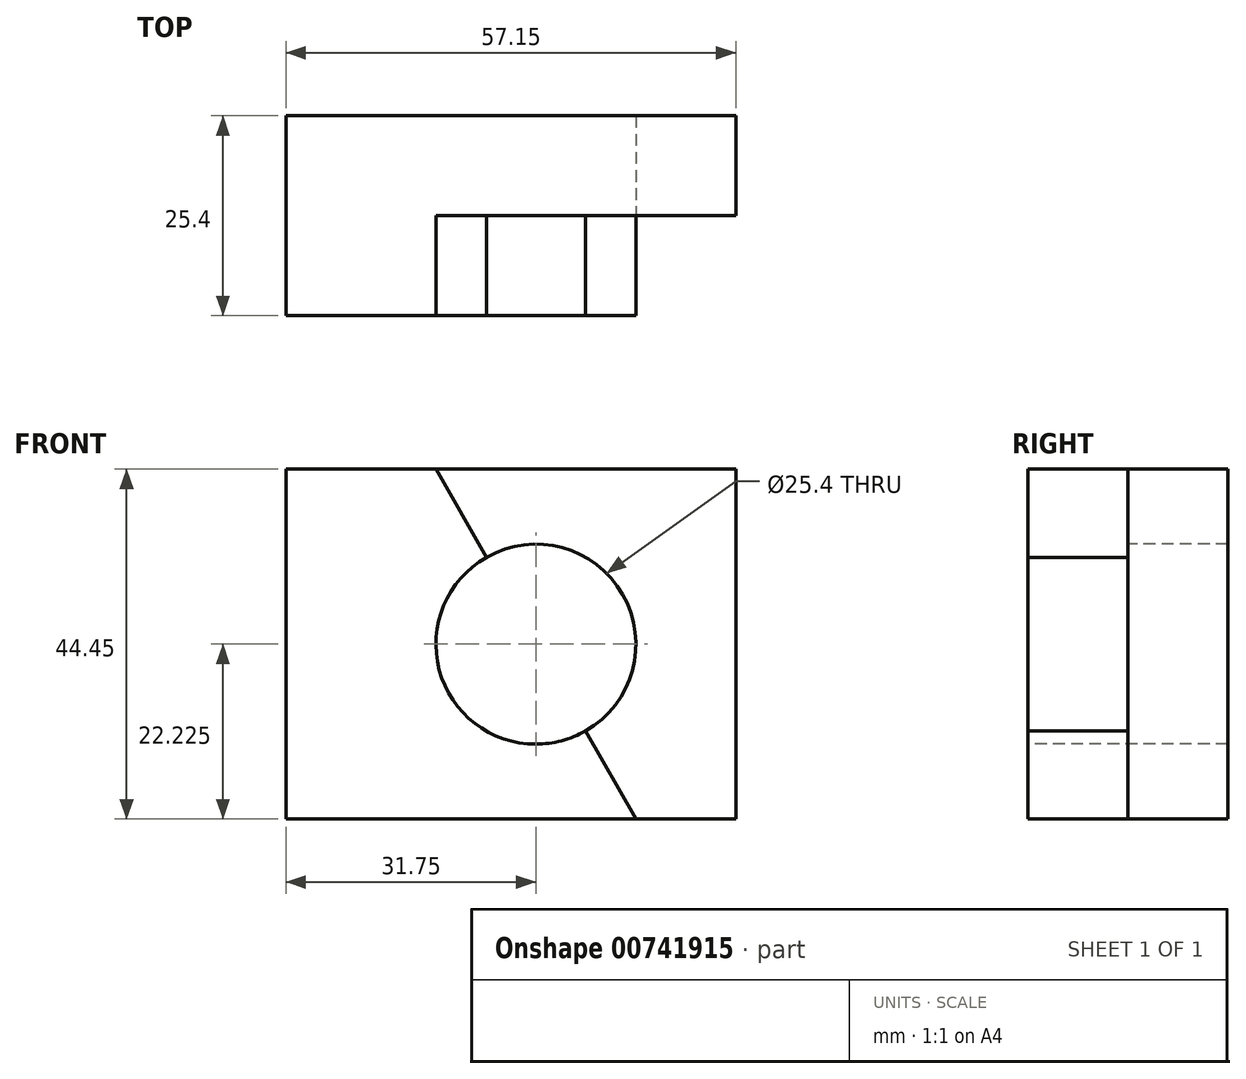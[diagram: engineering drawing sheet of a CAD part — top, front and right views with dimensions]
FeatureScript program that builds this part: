
annotation { "Feature Type Name" : "Feature", "Feature Type Description" : "" }
export const myFeature = defineFeature(function(context is Context, id is Id, definition is map)
    precondition{}
    {
        {
            var Q0;
            Q0=qCreatedBy(makeId("Front.planeOp"),FACE);
            var sketch = newSketch(context, id + "F0", { "sketchPlane" : qUnion([Q0])});
            skLineSegment(sketch, "E0", {"start": v(0, 0) * mm, "end": v(0, 44.45) * mm});
            skLineSegment(sketch, "E1", {"start": v(0, 44.45) * mm, "end": v(57.15, 44.45) * mm});
            skLineSegment(sketch, "E2", {"start": v(57.15, 44.45) * mm, "end": v(57.15, 0) * mm});
            skLineSegment(sketch, "E3", {"start": v(57.15, 0) * mm, "end": v(0, 0) * mm});
            skSolve(sketch);
        }
        {
            var Q0;
            Q0=makeQuery(id+"F0.imprint","IMPRINT",FACE,{"disambiguationData":[TD([[makeQuery(id+"F0.imprint","IMPRINT",EDGE,{"derivedFrom":sQuery(id+"F0.wireOp",EDGE,"E0")}),-1.0]])]});
            extrude(context, id + "F1", {"entities" : qUnion([Q0]), "depth" : 25.4 * mm, "offsetDistance" : 25.4 * mm});
        }
        {
            var Q0;
            Q0=makeQuery(id+"F1.opExtrude","CAP_FACE",FACE,{"disambiguationData":[OSD([sQuery(id+"F0.wireOp",EDGE,"E0"),sQuery(id+"F0.wireOp",EDGE,"E1"),sQuery(id+"F0.wireOp",EDGE,"E2"),sQuery(id+"F0.wireOp",EDGE,"E3")])],"isStart":false});
            var sketch = newSketch(context, id + "F2", { "sketchPlane" : qUnion([Q0])});
            skLineSegment(sketch, "E4", {"start": v(0, 44.45) * mm, "end": v(19.05, 44.45) * mm});
            skLineSegment(sketch, "E5", {"start": v(19.05, 44.45) * mm, "end": v(44.45, 0) * mm});
            skLineSegment(sketch, "E6", {"start": v(44.45, 0) * mm, "end": v(57.15, 0) * mm});
            skSolve(sketch);
        }
        {
            var Q0;
            {var subQ0=sQuery(id+"F2.wireOp",EDGE,"E5");Q0=makeQuery(id+"F2.imprint","IMPRINT",FACE,{"disambiguationData":[TD([[makeQuery(id+"F2.imprint","IMPRINT",EDGE,{"derivedFrom":subQ0}),1.0]])]});}
            extrude(context, id + "F3", {"entities" : qUnion([Q0]), "operationType" : NewBodyOperationType.REMOVE, "oppositeDirection" : true, "depth" : 12.7 * mm, "offsetDistance" : 25.4 * mm});
        }
        {
            var Q0;
            Q0=makeQuery(id+"F1.opExtrude","CAP_FACE",FACE,{"disambiguationData":[OSD([sQuery(id+"F0.wireOp",EDGE,"E0"),sQuery(id+"F0.wireOp",EDGE,"E1"),sQuery(id+"F0.wireOp",EDGE,"E2"),sQuery(id+"F0.wireOp",EDGE,"E3")])],"isStart":false});
            var sketch = newSketch(context, id + "F4", { "sketchPlane" : qUnion([Q0])});
            skCircle(sketch, "E7", {"center": v(31.75, 22.23) * mm, "radius": 12.7 * mm});
            skSolve(sketch);
        }
        {
            var Q0;
            {var subQ0=sQuery(id+"F4.wireOp",EDGE,"E7");var subQ1=makeQuery(id+"F3.boolean.opBoolean","COPY",EDGE,{"derivedFrom":makeQuery(id+"F3.opExtrude","CAP_EDGE",EDGE,{"disambiguationData":[OSD([sQuery(id+"F2.wireOp",EDGE,"E5")])],"isStart":true})});var subQ2=makeQuery(id+"F4.imprint","INTERSECT",VERTEX,{"disambiguationData":[OD(0.0)],"derivedFrom":[subQ1,subQ0]});Q0=makeQuery(id+"F4.imprint","IMPRINT",FACE,{"disambiguationData":[TD([[makeQuery(id+"F4.imprint","IMPRINT",EDGE,{"disambiguationData":[TD([[subQ2,-1.0]])],"derivedFrom":subQ0}),1.0]])]});}
            var Q1;
            {var subQ0=sQuery(id+"F4.wireOp",EDGE,"E7");var subQ1=makeQuery(id+"F3.boolean.opBoolean","COPY",EDGE,{"derivedFrom":makeQuery(id+"F3.opExtrude","CAP_EDGE",EDGE,{"disambiguationData":[OSD([sQuery(id+"F2.wireOp",EDGE,"E5")])],"isStart":true})});var subQ2=makeQuery(id+"F4.imprint","INTERSECT",VERTEX,{"disambiguationData":[OD(0.0)],"derivedFrom":[subQ1,subQ0]});Q1=makeQuery(id+"F4.imprint","IMPRINT",FACE,{"disambiguationData":[TD([[makeQuery(id+"F4.imprint","IMPRINT",EDGE,{"disambiguationData":[TD([[subQ2,1.0]])],"derivedFrom":subQ0}),1.0]])]});}
            extrude(context, id + "F5", {"entities" : qUnion([Q0, Q1]), "operationType" : NewBodyOperationType.REMOVE, "endBound" : BoundingType.THROUGH_ALL, "oppositeDirection" : true, "depth" : 25.4 * mm, "offsetDistance" : 25.4 * mm});
        }
    });
